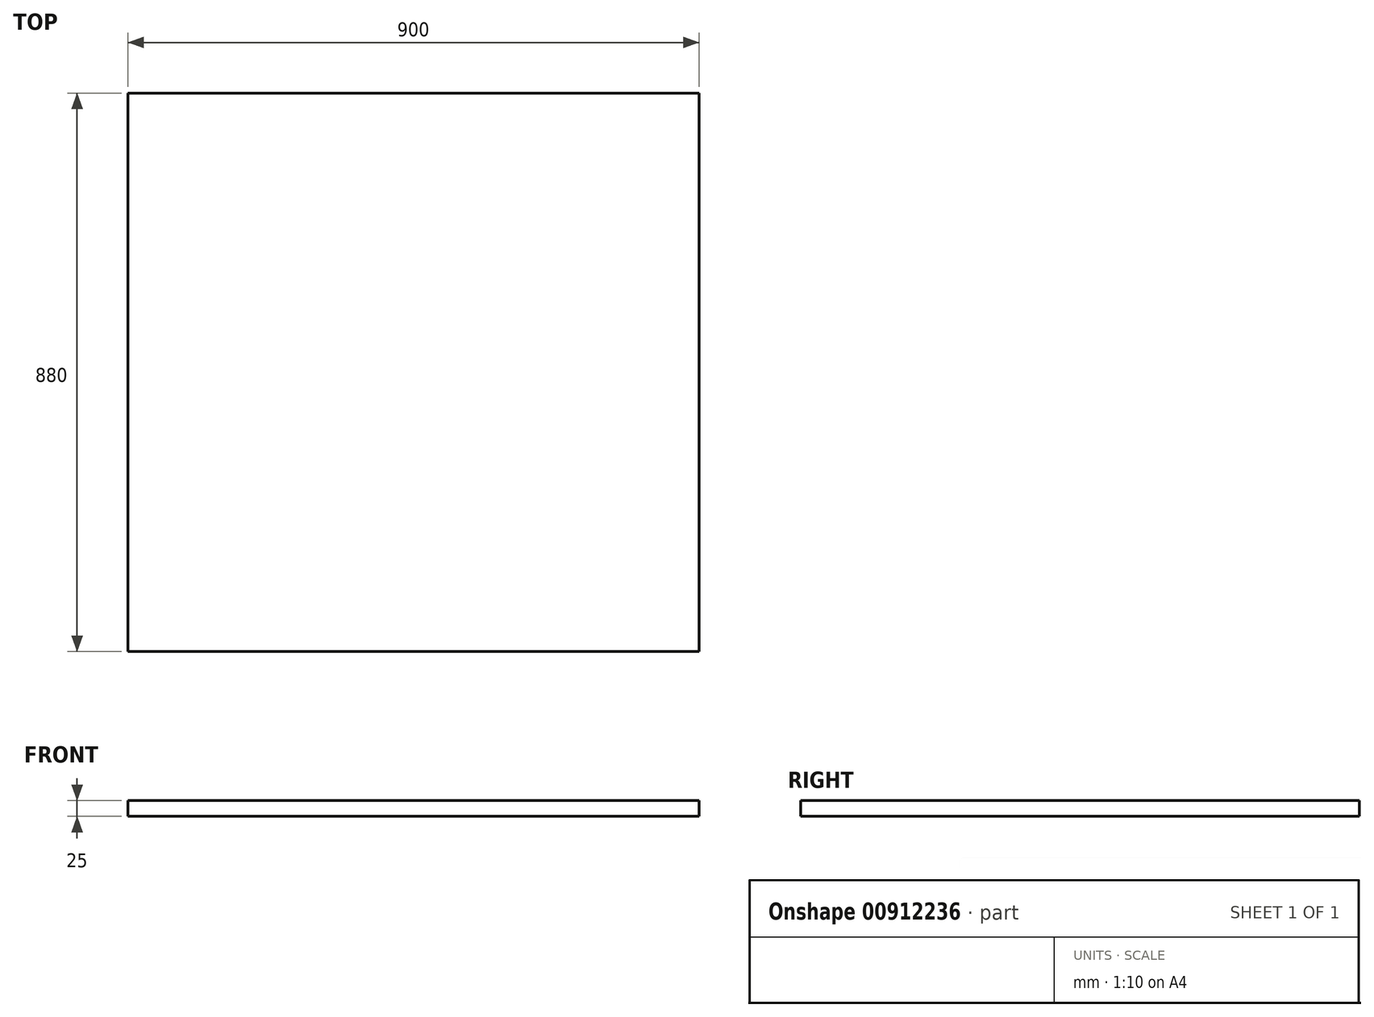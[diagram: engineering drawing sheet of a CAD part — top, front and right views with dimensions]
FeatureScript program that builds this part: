
annotation { "Feature Type Name" : "Feature", "Feature Type Description" : "" }
export const myFeature = defineFeature(function(context is Context, id is Id, definition is map)
    precondition{}
    {
        {
            var Q0;
            Q0=qCreatedBy(makeId("Top.planeOp"),FACE);
            var sketch = newSketch(context, id + "F0", { "sketchPlane" : qUnion([Q0])});
            skLineSegment(sketch, "E0.bottom", {"start": v(-39.59, 857.62) * mm, "end": v(860.41, 857.62) * mm});
            skLineSegment(sketch, "E0.top", {"start": v(-39.59, -22.38) * mm, "end": v(860.41, -22.38) * mm});
            skLineSegment(sketch, "E0.left", {"start": v(-39.59, 857.62) * mm, "end": v(-39.59, -22.38) * mm});
            skLineSegment(sketch, "E0.right", {"start": v(860.41, 857.62) * mm, "end": v(860.41, -22.38) * mm});
            skSolve(sketch);
        }
        {
            var Q0;
            Q0=qSketchRegion(id+"F0",true);
            extrude(context, id + "F1", {"entities" : qUnion([Q0]), "depth" : 25 * mm, "offsetDistance" : 25 * mm});
        }
    });
